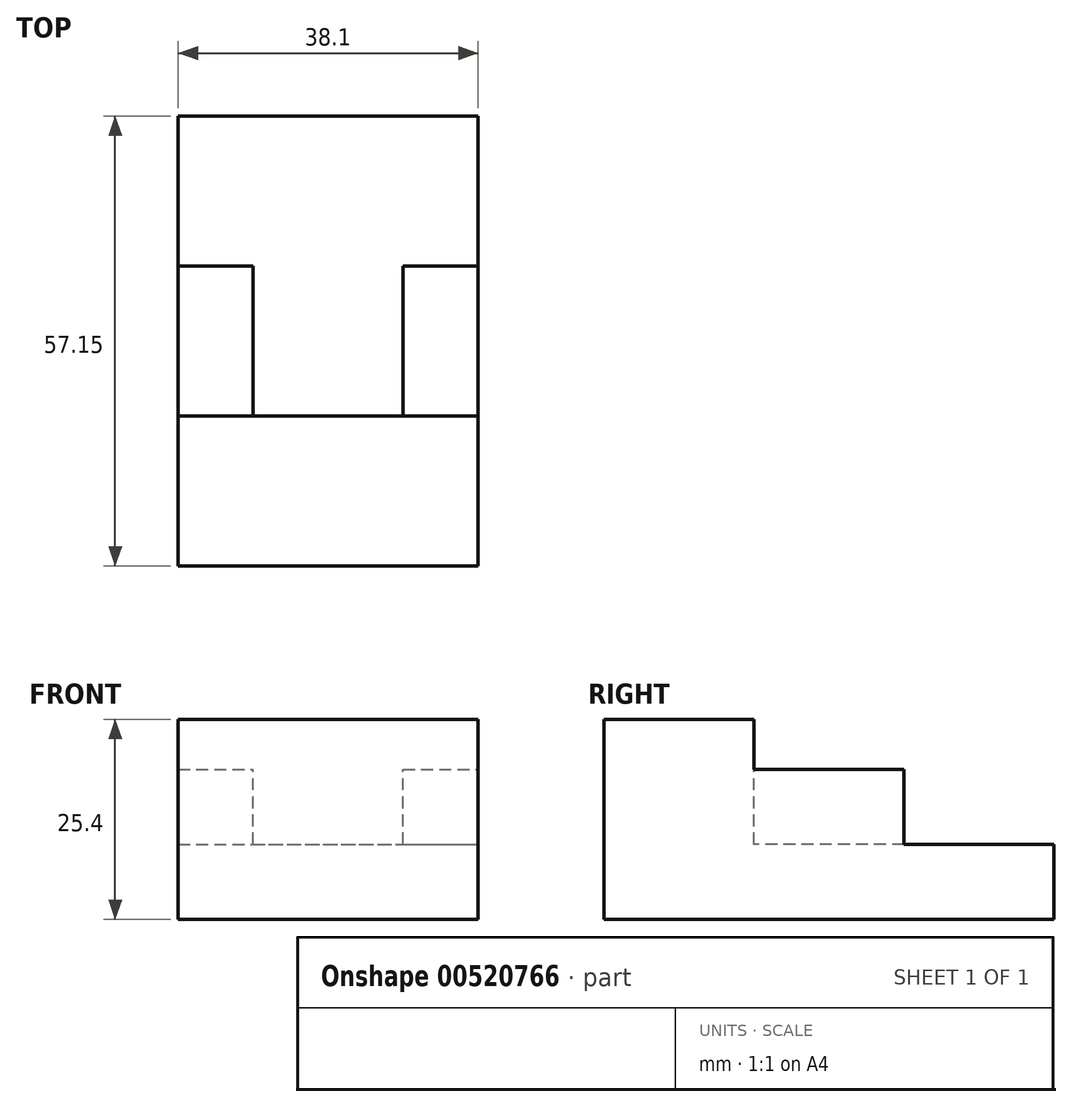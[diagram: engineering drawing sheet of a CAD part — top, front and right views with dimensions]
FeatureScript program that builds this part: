
annotation { "Feature Type Name" : "Feature", "Feature Type Description" : "" }
export const myFeature = defineFeature(function(context is Context, id is Id, definition is map)
    precondition{}
    {
        {
            var Q0;
            Q0=qCreatedBy(makeId("Top.planeOp"),FACE);
            var sketch = newSketch(context, id + "F0", { "sketchPlane" : qUnion([Q0])});
            skLineSegment(sketch, "E0.bottom", {"start": v(0, 0) * mm, "end": v(38.1, 0) * mm});
            skLineSegment(sketch, "E0.top", {"start": v(0, 57.15) * mm, "end": v(38.1, 57.15) * mm});
            skLineSegment(sketch, "E0.left", {"start": v(0, 0) * mm, "end": v(0, 57.15) * mm});
            skLineSegment(sketch, "E0.right", {"start": v(38.1, 0) * mm, "end": v(38.1, 57.15) * mm});
            skSolve(sketch);
        }
        {
            var Q0;
            Q0 = qSketchRegion(id + "F0", true);
            extrude(context, id + "F1", {"entities" : qUnion([Q0]), "depth" : 25.4 * mm, "offsetDistance" : 25.4 * mm});
        }
        {
            var Q0;
            Q0=makeQuery(id+"F1.opExtrude","SWEPT_FACE",FACE,{"disambiguationData":[OSD([sQuery(id+"F0.wireOp",EDGE,"E0.right")])]});
            var sketch = newSketch(context, id + "F2", { "sketchPlane" : qUnion([Q0])});
            skLineSegment(sketch, "E1", {"start": v(19.05, 25.4) * mm, "end": v(19.05, 19.05) * mm});
            skLineSegment(sketch, "E2", {"start": v(19.05, 19.05) * mm, "end": v(38.1, 19.05) * mm});
            skLineSegment(sketch, "E3", {"start": v(38.1, 19.05) * mm, "end": v(38.1, 9.53) * mm});
            skLineSegment(sketch, "E4", {"start": v(38.1, 9.53) * mm, "end": v(57.15, 9.53) * mm});
            skLineSegment(sketch, "E5", {"start": v(57.15, 9.53) * mm, "end": v(57.15, 25.4) * mm});
            skLineSegment(sketch, "E6", {"start": v(57.15, 25.4) * mm, "end": v(19.05, 25.4) * mm});
            skSolve(sketch);
        }
        {
            var Q0;
            Q0 = qSketchRegion(id + "F2", true);
            extrude(context, id + "F3", {"entities" : qUnion([Q0]), "operationType" : NewBodyOperationType.REMOVE, "endBound" : BoundingType.THROUGH_ALL, "oppositeDirection" : true, "depth" : 25.4 * mm, "offsetDistance" : 25.4 * mm});
        }
        {
            var Q0;
            Q0=makeQuery(id+"F3.boolean.opBoolean","COPY",FACE,{"derivedFrom":makeQuery(id+"F3.opExtrude","SWEPT_FACE",FACE,{"disambiguationData":[OSD([sQuery(id+"F2.wireOp",EDGE,"E2")])]})});
            var sketch = newSketch(context, id + "F4", { "sketchPlane" : qUnion([Q0])});
            skLineSegment(sketch, "E7.bottom", {"start": v(9.53, 38.1) * mm, "end": v(28.58, 38.1) * mm});
            skLineSegment(sketch, "E7.top", {"start": v(9.53, 19.05) * mm, "end": v(28.58, 19.05) * mm});
            skLineSegment(sketch, "E7.left", {"start": v(9.53, 38.1) * mm, "end": v(9.53, 19.05) * mm});
            skLineSegment(sketch, "E7.right", {"start": v(28.58, 38.1) * mm, "end": v(28.58, 19.05) * mm});
            skSolve(sketch);
        }
        {
            var Q0;
            Q0 = qSketchRegion(id + "F4", true);
            extrude(context, id + "F5", {"entities" : qUnion([Q0]), "operationType" : NewBodyOperationType.REMOVE, "oppositeDirection" : true, "depth" : 9.52 * mm, "offsetDistance" : 25.4 * mm});
        }
    });
